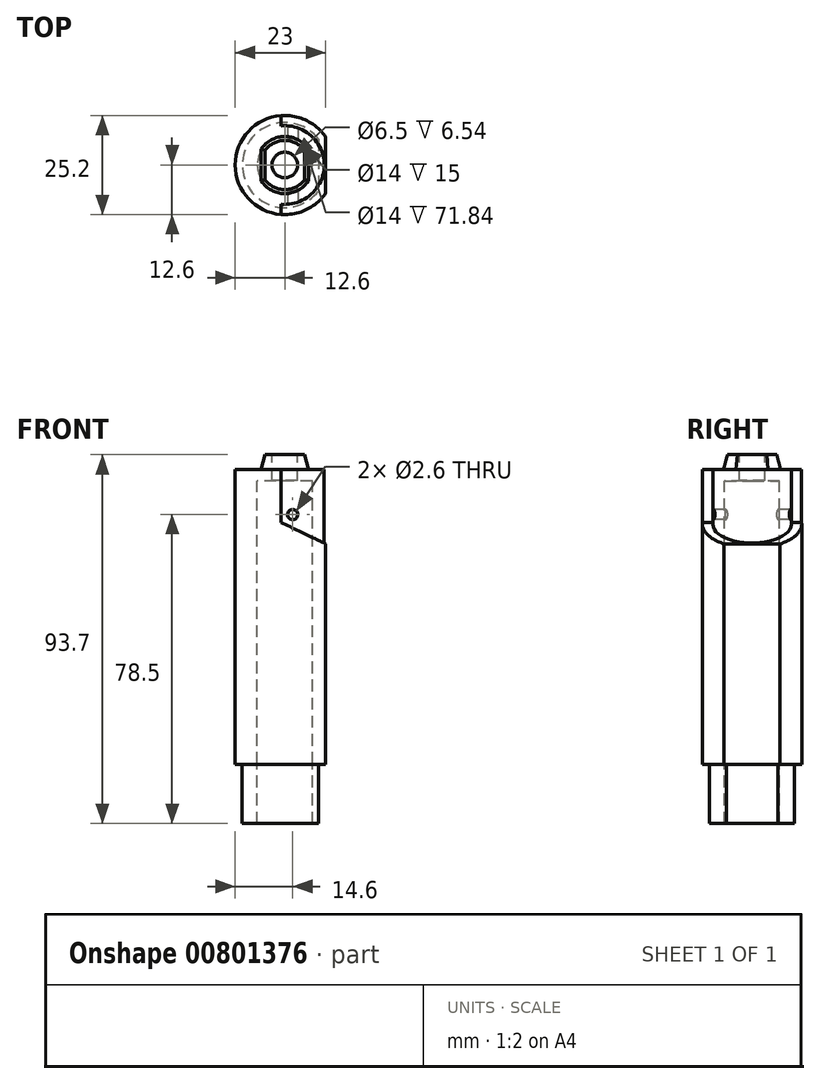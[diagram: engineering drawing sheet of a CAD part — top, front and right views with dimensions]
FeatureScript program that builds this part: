
annotation { "Feature Type Name" : "Feature", "Feature Type Description" : "" }
export const myFeature = defineFeature(function(context is Context, id is Id, definition is map)
    precondition{}
    {
        {
            var Q0;
            Q0=qCreatedBy(makeId("Top.planeOp"),FACE);
            var sketch = newSketch(context, id + "F0", { "sketchPlane" : qUnion([Q0])});
            skCircle(sketch, "E0", {"center": v(0, 0) * mm, "radius": 10 * mm});
            skCircle(sketch, "E1", {"center": v(0, 0) * mm, "radius": 12.6 * mm});
            skLineSegment(sketch, "E2", {"start": v(0, 12.6) * mm, "end": v(0, -12.6) * mm, "construction": true});
            skLineSegment(sketch, "E3", {"start": v(0, 12.6) * mm, "end": v(-1, 12.6) * mm, "construction": true});
            skLineSegment(sketch, "E4", {"start": v(-1, 12.56) * mm, "end": v(-1, 9.95) * mm});
            skPoint(sketch, "E5.orphan", {"position": v(-1, 12.6) * mm});
            skLineSegment(sketch, "E6", {"start": v(-12.6, 0) * mm, "end": v(12.6, 0) * mm, "construction": true});
            skLineSegment(sketch, "E7.MirrorCS", {"start": v(-1, -12.56) * mm, "end": v(-1, -9.95) * mm});
            skSolve(sketch);
        }
        {
            var Q0;
            {var subQ0=sQuery(id+"F0.wireOp",EDGE,"E4");Q0=makeQuery(id+"F0.imprint","IMPRINT",FACE,{"disambiguationData":[TD([[makeQuery(id+"F0.imprint","IMPRINT",EDGE,{"derivedFrom":subQ0}),-1.0]])]});}
            var Q1;
            {var subQ0=sQuery(id+"F0.wireOp",EDGE,"E0");var subQ1=makeQuery(id+"F0.imprint","INTERSECT",VERTEX,{"derivedFrom":[subQ0,sQuery(id+"F0.wireOp",EDGE,"E4")]});Q1=makeQuery(id+"F0.imprint","IMPRINT",FACE,{"disambiguationData":[TD([[makeQuery(id+"F0.imprint","IMPRINT",EDGE,{"disambiguationData":[TD([[subQ1,-1.0]])],"derivedFrom":subQ0}),1.0]])]});}
            extrude(context, id + "F1", {"entities" : qUnion([Q0, Q1]), "oppositeDirection" : true, "depth" : 13.5 * mm, "offsetDistance" : 25 * mm});
        }
        {
            var Q0;
            Q0=qCreatedBy(makeId("Top.planeOp"),FACE);
            cPlane(context, id + "F2", {"entities" : qUnion([Q0]), "cplaneType" : CPlaneType.OFFSET, "offset" : 20 * mm, "oppositeDirection" : true, "width" : 150 * mm, "height" : 150 * mm});
        }
        {
            var Q0;
            Q0=qCreatedBy(id+"F2.planeOp",FACE);
            var sketch = newSketch(context, id + "F3", { "sketchPlane" : qUnion([Q0])});
            skCircle(sketch, "E8", {"center": v(0, 0) * mm, "radius": 12.6 * mm});
            skSolve(sketch);
        }
        {
            var Q0;
            Q0=makeQuery(id+"F3.imprint","IMPRINT",FACE,{"disambiguationData":[TD([[makeQuery(id+"F3.imprint","IMPRINT",EDGE,{"derivedFrom":sQuery(id+"F3.wireOp",EDGE,"E8")}),1.0]])]});
            extrude(context, id + "F4", {"entities" : qUnion([Q0]), "operationType" : NewBodyOperationType.ADD, "depth" : 6.5 * mm, "offsetDistance" : 25 * mm});
        }
        {
            var Q0;
            Q0=qCreatedBy(makeId("Front.planeOp"),FACE);
            var sketch = newSketch(context, id + "F5", { "sketchPlane" : qUnion([Q0])});
            skLineSegment(sketch, "E9.0", {"start": v(-1, -13.5) * mm, "end": v(-1, 0) * mm});
            skLineSegment(sketch, "E10.0", {"start": v(-1, -13.5) * mm, "end": v(12.6, -13.5) * mm});
            skLineSegment(sketch, "E11.0", {"start": v(-12.6, -20) * mm, "end": v(12.6, -20) * mm});
            skLineSegment(sketch, "E12", {"start": v(-1, -13.5) * mm, "end": v(12.6, -20) * mm});
            skLineSegment(sketch, "E13", {"start": v(12.6, -13.5) * mm, "end": v(12.6, -20) * mm});
            skSolve(sketch);
        }
        {
            var Q0;
            Q0 = qSketchRegion(id + "F5", true);
            extrude(context, id + "F6", {"entities" : qUnion([Q0]), "operationType" : NewBodyOperationType.REMOVE, "endBound" : BoundingType.SYMMETRIC, "oppositeDirection" : true, "depth" : 30 * mm, "offsetDistance" : 25 * mm});
        }
        {
            var Q0;
            Q0=makeQuery(id+"F6.boolean.opBoolean","COPY",FACE,{"derivedFrom":makeQuery(id+"F6.opExtrude","SWEPT_FACE",FACE,{"disambiguationData":[OSD([sQuery(id+"F5.wireOp",EDGE,"E10.0")])]})});
            extrude(context, id + "F7", {"entities" : qUnion([Q0]), "operationType" : NewBodyOperationType.ADD, "depth" : 6.5 * mm, "offsetDistance" : 25 * mm});
        }
        {
            var Q0;
            Q0=makeQuery(id+"F4.opExtrude","CAP_FACE",FACE,{"disambiguationData":[OSD([sQuery(id+"F3.wireOp",EDGE,"E8")])],"isStart":true});
            extrude(context, id + "F8", {"entities" : qUnion([Q0]), "operationType" : NewBodyOperationType.ADD, "depth" : 70 * mm, "offsetDistance" : 25 * mm});
        }
        {
            var Q0;
            Q0=makeQuery(id+"F8.opExtrude","CAP_FACE",FACE,{"disambiguationData":[OSD([sQuery(id+"F3.wireOp",EDGE,"E8")])],"isStart":false});
            var sketch = newSketch(context, id + "F9", { "sketchPlane" : qUnion([Q0])});
            skLineSegment(sketch, "E14", {"start": v(-12.6, 0) * mm, "end": v(12.6, 0) * mm, "construction": true});
            skLineSegment(sketch, "E15", {"start": v(10.4, 0) * mm, "end": v(10.4, 7.11) * mm});
            skCircle(sketch, "E16.0", {"center": v(0, 0) * mm, "radius": 12.6 * mm});
            skLineSegment(sketch, "E17.MirrorCS", {"start": v(10.4, 0) * mm, "end": v(10.4, -7.11) * mm});
            skSolve(sketch);
        }
        {
            var Q0;
            {var subQ0=sQuery(id+"F9.wireOp",EDGE,"E15");Q0=makeQuery(id+"F9.imprint","IMPRINT",FACE,{"disambiguationData":[TD([[makeQuery(id+"F9.imprint","IMPRINT",EDGE,{"derivedFrom":subQ0}),-1.0]])]});}
            extrude(context, id + "F10", {"entities" : qUnion([Q0]), "operationType" : NewBodyOperationType.REMOVE, "oppositeDirection" : true, "depth" : 90 * mm, "offsetDistance" : 25 * mm});
        }
        {
            var Q0;
            Q0=makeQuery(id+"F8.opExtrude","CAP_FACE",FACE,{"disambiguationData":[OSD([sQuery(id+"F3.wireOp",EDGE,"E8")])],"isStart":false});
            var sketch = newSketch(context, id + "F11", { "sketchPlane" : qUnion([Q0])});
            skArc(sketch, "E18.0", {"start": v(10.4, -7.11) * mm, "mid": v(-12.6, 0) * mm, "end": v(10.4, 7.11) * mm});
            skLineSegment(sketch, "E19.0", {"start": v(10.4, -7.11) * mm, "end": v(10.4, 7.11) * mm});
            skArc(sketch, "E20.0", {"start": v(8.6, -6.53) * mm, "mid": v(-10.8, 0) * mm, "end": v(8.6, 6.53) * mm});
            skLineSegment(sketch, "E20.1", {"start": v(8.6, -6.53) * mm, "end": v(8.6, 6.53) * mm});
            skSolve(sketch);
        }
        {
            var Q0;
            Q0=makeQuery(id+"F11.imprint","IMPRINT",FACE,{"disambiguationData":[TD([[makeQuery(id+"F11.imprint","IMPRINT",EDGE,{"derivedFrom":sQuery(id+"F11.wireOp",EDGE,"E20.0")}),-1.0]])]});
            extrude(context, id + "F12", {"entities" : qUnion([Q0]), "operationType" : NewBodyOperationType.REMOVE, "oppositeDirection" : true, "depth" : 15 * mm, "offsetDistance" : 25 * mm});
        }
        {
            var Q0;
            Q0=makeQuery(id+"F1.opExtrude","CAP_FACE",FACE,{"disambiguationData":[OSD([sQuery(id+"F0.wireOp",EDGE,"E0"),sQuery(id+"F0.wireOp",EDGE,"E1"),sQuery(id+"F0.wireOp",EDGE,"E4"),sQuery(id+"F0.wireOp",EDGE,"E7.MirrorCS")])],"isStart":true});
            var sketch = newSketch(context, id + "F13", { "sketchPlane" : qUnion([Q0])});
            skArc(sketch, "E21", {"start": v(6, 4.07) * mm, "mid": v(0, 7.25) * mm, "end": v(-6, 4.07) * mm});
            skLineSegment(sketch, "E22", {"start": v(-7.25, 0) * mm, "end": v(7.25, 0) * mm, "construction": true});
            skLineSegment(sketch, "E23", {"start": v(6, 4.07) * mm, "end": v(6, 0) * mm});
            skLineSegment(sketch, "E24.MirrorCS", {"start": v(6, -4.07) * mm, "end": v(6, 0) * mm});
            skLineSegment(sketch, "E25", {"start": v(0, 7.25) * mm, "end": v(0, -7.25) * mm, "construction": true});
            skLineSegment(sketch, "E26.MirrorCS", {"start": v(-6, 4.07) * mm, "end": v(-6, 0) * mm});
            skLineSegment(sketch, "E27.MirrorCS", {"start": v(-6, -4.07) * mm, "end": v(-6, 0) * mm});
            skArc(sketch, "E28.trimOffspring", {"start": v(-6, -4.07) * mm, "mid": v(0, -7.25) * mm, "end": v(6, -4.07) * mm});
            skSolve(sketch);
        }
        {
            var Q0;
            Q0=makeQuery(id+"F13.imprint","IMPRINT",FACE,{"disambiguationData":[TD([[makeQuery(id+"F13.imprint","IMPRINT",EDGE,{"derivedFrom":sQuery(id+"F13.wireOp",EDGE,"E21")}),-1.0]])]});
            cPlane(context, id + "F14", {"entities" : qUnion([Q0]), "cplaneType" : CPlaneType.OFFSET, "offset" : 3.7 * mm, "width" : 150 * mm, "height" : 150 * mm});
        }
        {
            var Q0;
            Q0=qCreatedBy(id+"F14.planeOp",FACE);
            var sketch = newSketch(context, id + "F15", { "sketchPlane" : qUnion([Q0])});
            skArc(sketch, "E29.0", {"start": v(6, 4.07) * mm, "mid": v(0, 7.25) * mm, "end": v(-6, 4.07) * mm});
            skLineSegment(sketch, "E30.0", {"start": v(-6, 4.07) * mm, "end": v(-6, 0) * mm});
            skLineSegment(sketch, "E31.0", {"start": v(-6, -4.07) * mm, "end": v(-6, 0) * mm});
            skArc(sketch, "E32.0", {"start": v(-6, -4.07) * mm, "mid": v(0, -7.25) * mm, "end": v(6, -4.07) * mm});
            skLineSegment(sketch, "E33.0", {"start": v(6, -4.07) * mm, "end": v(6, 0) * mm});
            skLineSegment(sketch, "E34.0", {"start": v(6, 4.07) * mm, "end": v(6, 0) * mm});
            skLineSegment(sketch, "E35.0", {"start": v(5, 3.75) * mm, "end": v(5, 0) * mm});
            skLineSegment(sketch, "E35.1", {"start": v(-5, 3.75) * mm, "end": v(-5, 0) * mm});
            skLineSegment(sketch, "E35.2", {"start": v(-5, -3.75) * mm, "end": v(-5, 0) * mm});
            skArc(sketch, "E35.3", {"start": v(5, 3.75) * mm, "mid": v(0, 6.25) * mm, "end": v(-5, 3.75) * mm});
            skArc(sketch, "E35.4", {"start": v(-5, -3.75) * mm, "mid": v(0, -6.25) * mm, "end": v(5, -3.75) * mm});
            skLineSegment(sketch, "E35.5", {"start": v(5, -3.75) * mm, "end": v(5, 0) * mm});
            skSolve(sketch);
        }
        {
            var Q1;
            Q1=makeQuery(id+"F13.imprint","IMPRINT",FACE,{"disambiguationData":[TD([[makeQuery(id+"F13.imprint","IMPRINT",EDGE,{"derivedFrom":sQuery(id+"F13.wireOp",EDGE,"E21")}),1.0]])]});
            var Q2;
            Q2=makeQuery(id+"F15.imprint","IMPRINT",FACE,{"disambiguationData":[TD([[makeQuery(id+"F15.imprint","IMPRINT",EDGE,{"derivedFrom":sQuery(id+"F15.wireOp",EDGE,"E35.0")}),-1.0]])]});
            loft(context, id + "F16", {"operationType" : NewBodyOperationType.ADD, "sheetProfilesArray" : [{ "sheetProfileEntities" : qUnion([Q1]) }, { "sheetProfileEntities" : qUnion([Q2]) }]});
        }
        {
            var Q0;
            Q0=qCreatedBy(id+"F14.planeOp",FACE);
            var sketch = newSketch(context, id + "F17", { "sketchPlane" : qUnion([Q0])});
            skCircle(sketch, "E36", {"center": v(0, 0) * mm, "radius": 3.25 * mm});
            skSolve(sketch);
        }
        {
            var Q0;
            Q0=makeQuery(id+"F17.imprint","IMPRINT",FACE,{"disambiguationData":[TD([[makeQuery(id+"F17.imprint","IMPRINT",EDGE,{"derivedFrom":sQuery(id+"F17.wireOp",EDGE,"E36")}),1.0]])]});
            extrude(context, id + "F18", {"entities" : qUnion([Q0]), "operationType" : NewBodyOperationType.REMOVE, "endBound" : BoundingType.THROUGH_ALL, "oppositeDirection" : true, "depth" : 25 * mm, "offsetDistance" : 25 * mm});
        }
        {
            var Q0;
            Q0=makeQuery(id+"F1.opExtrude","CAP_FACE",FACE,{"disambiguationData":[OSD([sQuery(id+"F0.wireOp",EDGE,"E0"),sQuery(id+"F0.wireOp",EDGE,"E1"),sQuery(id+"F0.wireOp",EDGE,"E4"),sQuery(id+"F0.wireOp",EDGE,"E7.MirrorCS")])],"isStart":true});
            cPlane(context, id + "F19", {"entities" : qUnion([Q0]), "cplaneType" : CPlaneType.OFFSET, "offset" : 3 * mm, "oppositeDirection" : true, "width" : 150 * mm, "height" : 150 * mm});
        }
        {
            var Q0;
            Q0=qCreatedBy(id+"F19.planeOp",FACE);
            var sketch = newSketch(context, id + "F20", { "sketchPlane" : qUnion([Q0])});
            skCircle(sketch, "E37", {"center": v(0, 0) * mm, "radius": 7 * mm});
            skSolve(sketch);
        }
        {
            var Q0;
            Q0 = qSketchRegion(id + "F20", true);
            extrude(context, id + "F21", {"entities" : qUnion([Q0]), "operationType" : NewBodyOperationType.REMOVE, "oppositeDirection" : true, "depth" : 90 * mm, "offsetDistance" : 25 * mm});
        }
        {
            var Q0;
            Q0=makeQuery(id+"F12.boolean.opBoolean","COPY",FACE,{"derivedFrom":makeQuery(id+"F12.opExtrude","CAP_FACE",FACE,{"disambiguationData":[OSD([sQuery(id+"F11.wireOp",EDGE,"E20.0"),sQuery(id+"F11.wireOp",EDGE,"E20.1")])],"isStart":false})});
            var sketch = newSketch(context, id + "F22", { "sketchPlane" : qUnion([Q0])});
            skCircle(sketch, "E38.0", {"center": v(0, 0) * mm, "radius": 7 * mm});
            skSolve(sketch);
        }
        {
            var Q0;
            Q0 = qSketchRegion(id + "F22", true);
            extrude(context, id + "F23", {"entities" : qUnion([Q0]), "operationType" : NewBodyOperationType.ADD, "oppositeDirection" : true, "depth" : 0.16 * mm, "offsetDistance" : 25 * mm});
        }
        {
            var Q0;
            Q0=qCreatedBy(id+"F19.planeOp",FACE);
            var sketch = newSketch(context, id + "F24", { "sketchPlane" : qUnion([Q0])});
            skCircle(sketch, "E39.0", {"center": v(0, 0) * mm, "radius": 7 * mm});
            skSolve(sketch);
        }
        {
            var Q0;
            Q0 = qSketchRegion(id + "F24", true);
            extrude(context, id + "F25", {"entities" : qUnion([Q0]), "operationType" : NewBodyOperationType.ADD, "depth" : .16 * mm, "offsetDistance" : 25 * mm});
        }
        {
            var Q0;
            Q0=qCreatedBy(makeId("Front.planeOp"),FACE);
            var sketch = newSketch(context, id + "F26", { "sketchPlane" : qUnion([Q0])});
            skCircle(sketch, "E40", {"center": v(2, -11.5) * mm, "radius": 1.3 * mm});
            skSolve(sketch);
        }
        {
            var Q0;
            Q0 = qSketchRegion(id + "F26", true);
            extrude(context, id + "F27", {"entities" : qUnion([Q0]), "operationType" : NewBodyOperationType.REMOVE, "endBound" : BoundingType.SYMMETRIC, "oppositeDirection" : true, "depth" : 25 * mm, "offsetDistance" : 25 * mm});
        }
    });
